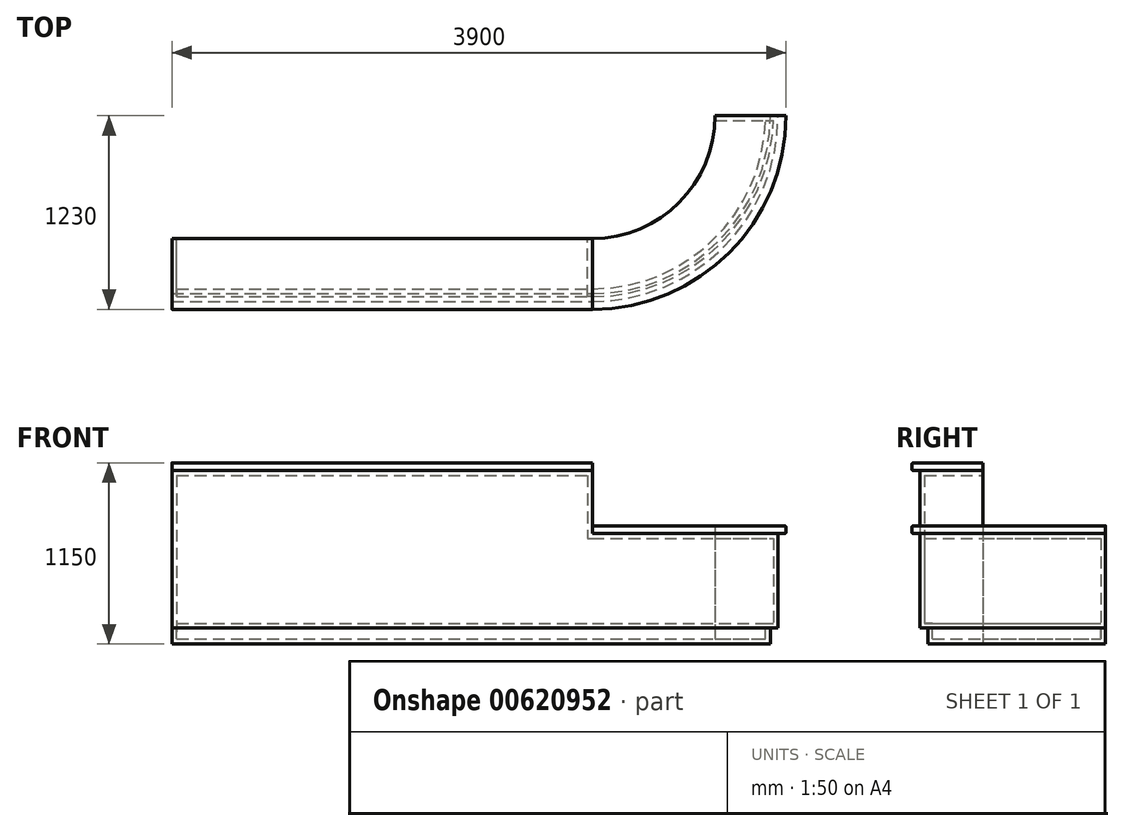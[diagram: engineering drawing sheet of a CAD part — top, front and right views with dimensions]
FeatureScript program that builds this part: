
annotation { "Feature Type Name" : "Feature", "Feature Type Description" : "" }
export const myFeature = defineFeature(function(context is Context, id is Id, definition is map)
    precondition{}
    {
        {
            var Q0;
            Q0=qCreatedBy(makeId("Top.planeOp"),FACE);
            var sketch = newSketch(context, id + "F0", { "sketchPlane" : qUnion([Q0])});
            skLineSegment(sketch, "E0", {"start": v(-1335, 0) * mm, "end": v(1335, 0) * mm});
            skLineSegment(sketch, "E1", {"start": v(-1335, 0) * mm, "end": v(-1335, 400) * mm});
            skLineSegment(sketch, "E2", {"start": v(-1335, 400) * mm, "end": v(1335, 400) * mm});
            skLineSegment(sketch, "E3", {"start": v(1335, 400) * mm, "end": v(1335, 1180) * mm, "construction": true});
            skArc(sketch, "E4", {"start": v(1335, 400) * mm, "mid": v(1886.54, 628.46) * mm, "end": v(2115, 1180) * mm});
            skArc(sketch, "E5.0", {"start": v(1335, 0) * mm, "mid": v(2169.39, 345.61) * mm, "end": v(2515, 1180) * mm});
            skLineSegment(sketch, "E6", {"start": v(2115, 1180) * mm, "end": v(2515, 1180) * mm});
            skSolve(sketch);
        }
        {
            var Q0;
            Q0 = qSketchRegion(id + "F0", true);
            extrude(context, id + "F1", {"entities" : qUnion([Q0]), "depth" : 700 * mm, "offsetDistance" : 25 * mm});
        }
        {
            var Q0;
            Q0=makeQuery(id+"F1.opExtrude","CAP_FACE",FACE,{"disambiguationData":[OSD([sQuery(id+"F0.wireOp",EDGE,"E0"),sQuery(id+"F0.wireOp",EDGE,"E1"),sQuery(id+"F0.wireOp",EDGE,"E2"),sQuery(id+"F0.wireOp",EDGE,"E4"),sQuery(id+"F0.wireOp",EDGE,"E5.0"),sQuery(id+"F0.wireOp",EDGE,"E6")])],"isStart":false});
            var sketch = newSketch(context, id + "F2", { "sketchPlane" : qUnion([Q0])});
            skLineSegment(sketch, "E7.0", {"start": v(-1335, 0) * mm, "end": v(-1335, 400) * mm});
            skLineSegment(sketch, "E8.0", {"start": v(-1335, 400) * mm, "end": v(1335, 400) * mm});
            skLineSegment(sketch, "E9.0", {"start": v(-1335, 0) * mm, "end": v(1335, 0) * mm});
            skLineSegment(sketch, "E10", {"start": v(1335, 0) * mm, "end": v(1335, 400) * mm});
            skSolve(sketch);
        }
        {
            var Q0;
            Q0 = qSketchRegion(id + "F2", true);
            extrude(context, id + "F3", {"entities" : qUnion([Q0]), "operationType" : NewBodyOperationType.ADD, "depth" : 400 * mm, "offsetDistance" : 25 * mm});
        }
        {
            var Q0;
            Q0=makeQuery(id+"F3.opExtrude","CAP_FACE",FACE,{"disambiguationData":[OSD([sQuery(id+"F2.wireOp",EDGE,"E7.0"),sQuery(id+"F2.wireOp",EDGE,"E8.0"),sQuery(id+"F2.wireOp",EDGE,"E9.0"),sQuery(id+"F2.wireOp",EDGE,"E10")])],"isStart":false});
            var sketch = newSketch(context, id + "F4", { "sketchPlane" : qUnion([Q0])});
            skLineSegment(sketch, "E11.0.0", {"start": v(-1335, 0) * mm, "end": v(1335, 0) * mm, "construction": true});
            skLineSegment(sketch, "E11.0.1", {"start": v(1335, -50) * mm, "end": v(1335, 400) * mm});
            skLineSegment(sketch, "E11.0.2", {"start": v(1335, 400) * mm, "end": v(-1335, 400) * mm});
            skLineSegment(sketch, "E11.0.3", {"start": v(-1335, 400) * mm, "end": v(-1335, -50) * mm});
            skLineSegment(sketch, "E12.0", {"start": v(-1335, -50) * mm, "end": v(1335, -50) * mm});
            skSolve(sketch);
        }
        {
            var Q0;
            Q0 = qSketchRegion(id + "F4", true);
            var Q1;
            Q1=sQuery(id+"F4.wireOp",EDGE,"E11.0.0");
            extrude(context, id + "F5", {"entities" : qUnion([Q0]), "surfaceEntities" : qUnion([Q1]), "depth" : 50 * mm, "offsetDistance" : 25 * mm});
        }
        {
            var Q0;
            Q0=makeQuery(id+"F1.opExtrude","CAP_FACE",FACE,{"disambiguationData":[OSD([sQuery(id+"F0.wireOp",EDGE,"E0"),sQuery(id+"F0.wireOp",EDGE,"E1"),sQuery(id+"F0.wireOp",EDGE,"E2"),sQuery(id+"F0.wireOp",EDGE,"E4"),sQuery(id+"F0.wireOp",EDGE,"E5.0"),sQuery(id+"F0.wireOp",EDGE,"E6")])],"isStart":false});
            var sketch = newSketch(context, id + "F6", { "sketchPlane" : qUnion([Q0])});
            skArc(sketch, "E13.0", {"start": v(1335, 400) * mm, "mid": v(1886.54, 628.46) * mm, "end": v(2115, 1180) * mm});
            skLineSegment(sketch, "E14.0", {"start": v(2115, 1180) * mm, "end": v(2565, 1180) * mm});
            skLineSegment(sketch, "E15.0", {"start": v(1335, -50) * mm, "end": v(1335, 400) * mm});
            skArc(sketch, "E16.0", {"start": v(1335, -50) * mm, "mid": v(2204.74, 310.26) * mm, "end": v(2565, 1180) * mm});
            skPoint(sketch, "E17.orphan", {"position": v(1335, 0) * mm});
            skPoint(sketch, "E18.orphan", {"position": v(2515, 1180) * mm});
            skSolve(sketch);
        }
        {
            var Q0;
            Q0 = qSketchRegion(id + "F6", true);
            extrude(context, id + "F7", {"entities" : qUnion([Q0]), "depth" : 50 * mm, "offsetDistance" : 25 * mm});
        }
        {
            var Q0;
            Q0=qCreatedBy(makeId("Top.planeOp"),FACE);
            var sketch = newSketch(context, id + "F8", { "sketchPlane" : qUnion([Q0])});
            skLineSegment(sketch, "E19.0", {"start": v(-1335, 0) * mm, "end": v(1335, 0) * mm});
            skArc(sketch, "E20.0", {"start": v(1335, 0) * mm, "mid": v(2169.39, 345.61) * mm, "end": v(2515, 1180) * mm});
            skSolve(sketch);
        }
        {
            var Q0;
            Q0=makeQuery(id+"F3.boolean.opBoolean","MERGE",FACE,{"derivedFrom":[makeQuery(id+"F1.opExtrude","SWEPT_FACE",FACE,{"disambiguationData":[OSD([sQuery(id+"F0.wireOp",EDGE,"E1")])]}),makeQuery(id+"F3.opExtrude","SWEPT_FACE",FACE,{"disambiguationData":[OSD([sQuery(id+"F2.wireOp",EDGE,"E7.0")])]})]});
            var sketch = newSketch(context, id + "F9", { "sketchPlane" : qUnion([Q0])});
            skLineSegment(sketch, "E21.bottom", {"start": v(0, 0) * mm, "end": v(-50, 0) * mm});
            skLineSegment(sketch, "E21.top", {"start": v(0, 100) * mm, "end": v(-50, 100) * mm});
            skLineSegment(sketch, "E21.left", {"start": v(0, 0) * mm, "end": v(0, 100) * mm});
            skLineSegment(sketch, "E21.right", {"start": v(-50, 0) * mm, "end": v(-50, 100) * mm});
            skSolve(sketch);
        }
        {
            var Q0;
            Q0 = qSketchRegion(id + "F9", true);
            var Q1;
            Q1 = qConstructionFilter(qBodyType(qCreatedBy(id + "F8" ,EDGE), BodyType.WIRE), ConstructionObject.NO);
            sweep(context, id + "F10", {"operationType" : NewBodyOperationType.REMOVE, "profiles" : qUnion([Q0]), "path" : qUnion([Q1])});
        }
        {
            var Q0;
            Q0=makeQuery(id+"F3.boolean.opBoolean","MERGE",FACE,{"derivedFrom":[makeQuery(id+"F1.opExtrude","SWEPT_FACE",FACE,{"disambiguationData":[OSD([sQuery(id+"F0.wireOp",EDGE,"E2")])]}),makeQuery(id+"F3.opExtrude","SWEPT_FACE",FACE,{"disambiguationData":[OSD([sQuery(id+"F2.wireOp",EDGE,"E8.0")])]})]});
            var Q1;
            Q1=makeQuery(id+"F1.opExtrude","SWEPT_FACE",FACE,{"disambiguationData":[OSD([sQuery(id+"F0.wireOp",EDGE,"E4")])]});
            shell(context, id + "F11", {"entities" : qUnion([Q0, Q1]), "thickness" : 30 * mm});
        }
        {
            var Q0;
            Q0=makeQuery(id+"F5.opExtrude","CAP_EDGE",EDGE,{"disambiguationData":[OSD([sQuery(id+"F4.wireOp",EDGE,"E12.0")])],"isStart":false});
            var Q1;
            Q1=makeQuery(id+"F5.opExtrude","CAP_EDGE",EDGE,{"disambiguationData":[OSD([sQuery(id+"F4.wireOp",EDGE,"E12.0")])],"isStart":true});
            var Q2;
            Q2=makeQuery(id+"F7.opExtrude","CAP_EDGE",EDGE,{"disambiguationData":[OSD([sQuery(id+"F6.wireOp",EDGE,"E16.0")])],"isStart":false});
            var Q3;
            Q3=makeQuery(id+"F7.opExtrude","CAP_EDGE",EDGE,{"disambiguationData":[OSD([sQuery(id+"F6.wireOp",EDGE,"E16.0")])],"isStart":true});
            fillet(context, id + "F12", {"entities" : qUnion([Q0, Q1, Q2, Q3]), "radius" : 10 * mm, "tangentPropagation" : true, "allowEdgeOverflow" : false});
        }
    });
